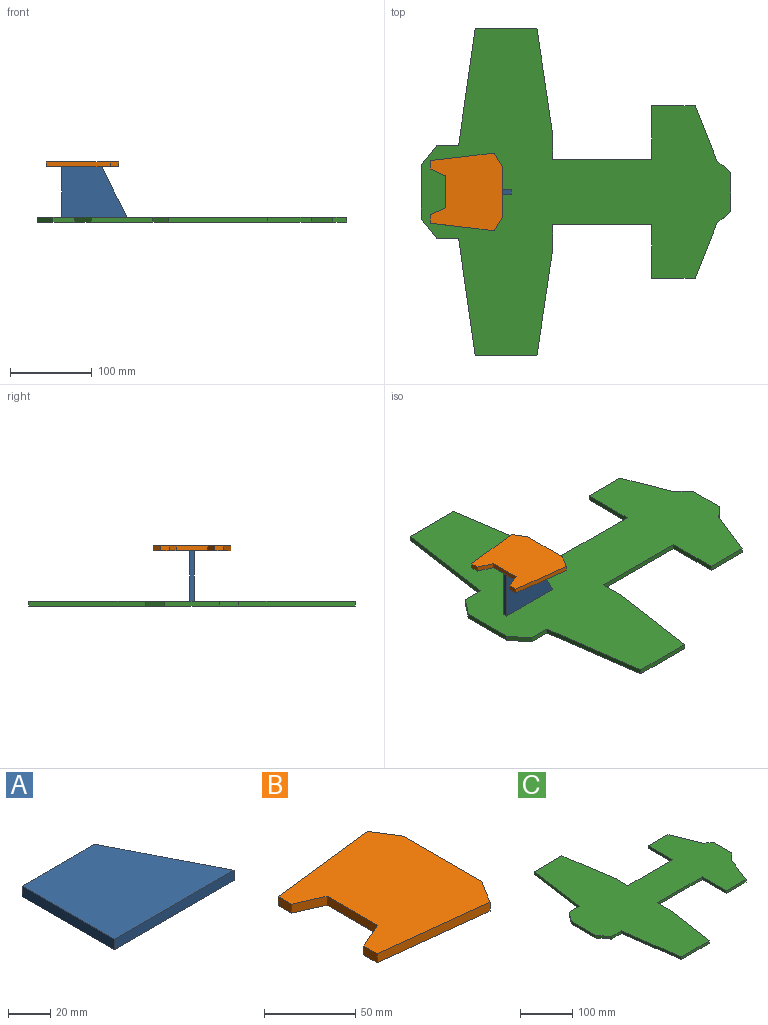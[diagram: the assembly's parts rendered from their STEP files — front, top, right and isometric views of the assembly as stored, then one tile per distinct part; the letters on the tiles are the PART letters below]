
ASSEMBLY  parts=3 mates=2
PART A: 6 faces, bbox 80x61.6x6 mm
  f0: plane 61.57x6mm, normal (-1,0,0), area 369.4mm2, adj f1,f3,f4,f5
  f1: plane 80x6mm, normal (0,-1,0), area 480mm2, adj f0,f2,f4,f5
  f2: plane 61.57x31.51mm, normal (0.89,0.46,0), area 415mm2, adj f1,f3,f4,f5
  f3: plane 48.49x6mm, normal (0,1,0), area 290.9mm2, adj f0,f2,f4,f5
  f4: plane 80x61.57mm, normal (0,0,1), area 3955.7mm2, adj f0,f1,f2,f3
  f5: plane 80x61.57mm, normal (0,0,-1), area 3955.7mm2, adj f0,f1,f2,f3
PART B: 12 faces, bbox 89x95.1x6 mm
  f0: plane 39.12x6mm, normal (-1,0,0), area 234.7mm2, adj f1,f6,f7,f8
  f1: plane 19.18x8.44mm, normal (-0.4,0.92,0), area 125.7mm2, adj f0,f2,f6,f7
  f2: plane 10.36x6mm, normal (-1,0,0), area 62.1mm2, adj f1,f3,f6,f7
  f3: plane 78.24x9.21mm, normal (-0.12,-0.99,0), area 472.7mm2, adj f2,f4,f6,f7
  f4: plane 17.26x10.74mm, normal (0.85,-0.53,0), area 122mm2, adj f3,f5,f6,f7
  f5: plane 60.6x6mm, normal (1,0,0), area 363.6mm2, adj f4,f6,f7,f11
  f6: plane 95.12x88.98mm, normal (0,0,1), area 6645.9mm2, adj f0,f1,f2,f3,f4,f5,f8,f9
  f7: plane 95.12x88.98mm, normal (0,0,-1), area 6645.9mm2, adj f0,f1,f2,f3,f4,f5,f8,f9
  f8: plane 19.18x8.44mm, normal (-0.4,-0.92,0), area 125.7mm2, adj f0,f6,f7,f9
  f9: plane 10.36x6mm, normal (-1,0,0), area 62.1mm2, adj f6,f7,f8,f10
  f10: plane 78.24x9.21mm, normal (-0.12,0.99,0), area 472.7mm2, adj f6,f7,f9,f11
  f11: plane 17.26x10.74mm, normal (0.85,0.53,0), area 122mm2, adj f5,f6,f7,f10
PART C: 26 faces, bbox 378.6x400x6 mm
  f0: plane 121.5x6mm, normal (0,-1,0), area 729mm2, adj f1,f12,f13,f14
  f1: plane 65.69x6mm, normal (-1,0,0), area 394.1mm2, adj f0,f2,f13,f14
  f2: plane 53.16x6mm, normal (0,-1,0), area 318.9mm2, adj f1,f3,f13,f14
  f3: plane 66.72x26.58mm, normal (0.93,-0.37,0), area 430.9mm2, adj f2,f4,f13,f14
  f4: plane 16.81x15.73mm, normal (0.68,-0.73,0), area 138.2mm2, adj f3,f5,f13,f14
  f5: plane 46.76x6mm, normal (1,0,0), area 280.6mm2, adj f4,f13,f14,f19
  f6: plane 66.18x6mm, normal (-1,0,0), area 397.1mm2, adj f7,f13,f14,f20
  f7: plane 24.41x18.98mm, normal (-0.79,-0.61,0), area 185.5mm2, adj f6,f8,f13,f14
  f8: plane 26.58x6mm, normal (0,-1,0), area 159.5mm2, adj f7,f9,f13,f14
  f9: plane 142.48x20.21mm, normal (-0.99,-0.14,0), area 863.4mm2, adj f8,f10,f13,f14
  f10: plane 75.71x6mm, normal (0,-1,0), area 454.3mm2, adj f9,f11,f13,f14
  f11: plane 128.38x19.06mm, normal (0.99,-0.15,0), area 778.7mm2, adj f10,f12,f13,f14
  f12: plane 31.46x6mm, normal (1,0,0), area 188.8mm2, adj f0,f11,f13,f14
  f13: plane 399.95x378.6mm, normal (0,0,1), area 71345.9mm2, adj f0,f1,f2,f3,f4,f5,f6,f7
  f14: plane 399.95x378.6mm, normal (0,0,-1), area 71345.9mm2, adj f0,f1,f2,f3,f4,f5,f6,f7
  f15: plane 121.5x6mm, normal (0,1,0), area 729mm2, adj f13,f14,f16,f25
  f16: plane 65.69x6mm, normal (-1,0,0), area 394.1mm2, adj f13,f14,f15,f17
  f17: plane 53.16x6mm, normal (0,1,0), area 318.9mm2, adj f13,f14,f16,f18
  f18: plane 66.72x26.58mm, normal (0.93,0.37,0), area 430.9mm2, adj f13,f14,f17,f19
  f19: plane 16.81x15.73mm, normal (0.68,0.73,0), area 138.2mm2, adj f5,f13,f14,f18
  f20: plane 24.41x18.98mm, normal (-0.79,0.61,0), area 185.5mm2, adj f6,f13,f14,f21
  f21: plane 26.58x6mm, normal (0,1,0), area 159.5mm2, adj f13,f14,f20,f22
  f22: plane 142.48x20.21mm, normal (-0.99,0.14,0), area 863.4mm2, adj f13,f14,f21,f23
  f23: plane 75.71x6mm, normal (0,1,0), area 454.3mm2, adj f13,f14,f22,f24
  f24: plane 128.38x19.06mm, normal (0.99,0.15,0), area 778.7mm2, adj f13,f14,f23,f25
  f25: plane 31.46x6mm, normal (1,0,0), area 188.8mm2, adj f13,f14,f15,f24
PLACE A rot(axis=(1,0,0),90deg) t=(-10.56,99.79,19.36)mm
PLACE B t=(-120.66,-51.34,80.93)mm
PLACE C t=(-40.56,96.79,13.36)mm
MATE fastened B.f7 <-> A.f3  axis (0,0,-1) through (-10.56,96.79,80.93)mm
MATE fastened A.f1 <-> C.f13  axis (0,0,-1) through (-10.56,96.79,19.36)mm
